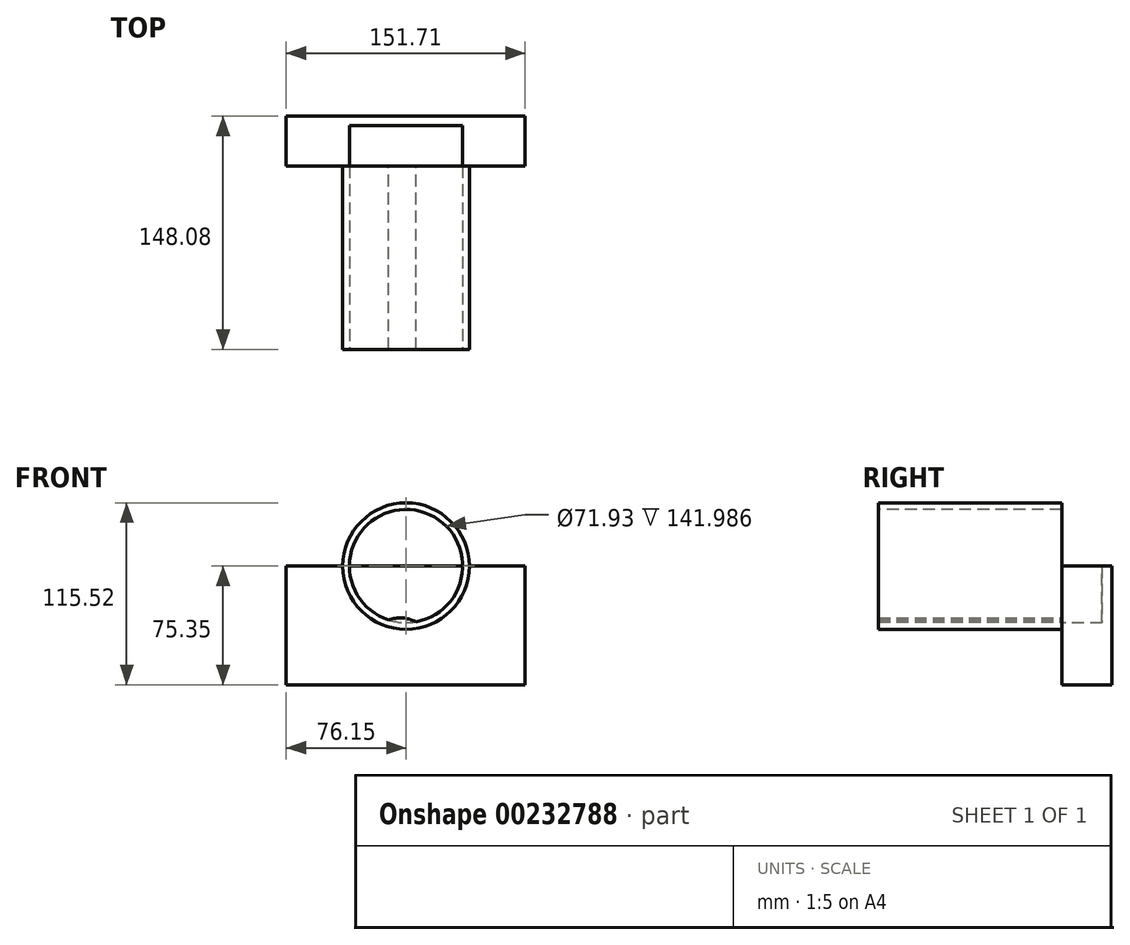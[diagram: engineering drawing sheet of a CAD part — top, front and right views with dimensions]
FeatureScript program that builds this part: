
annotation { "Feature Type Name" : "Feature", "Feature Type Description" : "" }
export const myFeature = defineFeature(function(context is Context, id is Id, definition is map)
    precondition{}
    {
        {
            var Q0;
            Q0=qCreatedBy(makeId("Front.planeOp"),FACE);
            var sketch = newSketch(context, id + "F0", { "sketchPlane" : qUnion([Q0])});
            skCircle(sketch, "E0", {"center": v(0, 0) * mm, "radius": 40.17 * mm});
            skSolve(sketch);
        }
        {
            var Q0;
            Q0=makeQuery(id+"F0.imprint","IMPRINT",FACE,{"disambiguationData":[TD([[makeQuery(id+"F0.imprint","IMPRINT",EDGE,{"derivedFrom":sQuery(id+"F0.wireOp",EDGE,"E0")}),1.0]])]});
            extrude(context, id + "F1", {"entities" : qUnion([Q0]), "depth" : 116.33 * mm});
        }
        {
            var Q0;
            Q0=makeQuery(id+"F1.opExtrude","CAP_FACE",FACE,{"disambiguationData":[OSD([sQuery(id+"F0.wireOp",EDGE,"E0")])],"isStart":false});
            var sketch = newSketch(context, id + "F2", { "sketchPlane" : qUnion([Q0])});
            skCircle(sketch, "E1", {"center": v(0, 0) * mm, "radius": 35.97 * mm});
            skSolve(sketch);
        }
        {
            var Q0;
            Q0=makeQuery(id+"F2.imprint","IMPRINT",FACE,{"disambiguationData":[TD([[makeQuery(id+"F2.imprint","IMPRINT",EDGE,{"derivedFrom":sQuery(id+"F2.wireOp",EDGE,"E1")}),1.0]])]});
            extrude(context, id + "F3", {"entities" : qUnion([Q0]), "operationType" : NewBodyOperationType.REMOVE, "endBound" : BoundingType.THROUGH_ALL, "oppositeDirection" : true, "depth" : 25.4 * mm});
        }
        {
            var Q0;
            Q0=qCreatedBy(makeId("Front.planeOp"),FACE);
            var sketch = newSketch(context, id + "F4", { "sketchPlane" : qUnion([Q0])});
            skLineSegment(sketch, "E2.bottom", {"start": v(0, 0) * mm, "end": v(75.56, 0) * mm});
            skLineSegment(sketch, "E2.top", {"start": v(0, 75.75) * mm, "end": v(75.56, 75.75) * mm});
            skLineSegment(sketch, "E2.left", {"start": v(0, 0) * mm, "end": v(0, 75.75) * mm});
            skLineSegment(sketch, "E2.right", {"start": v(75.56, 0) * mm, "end": v(75.56, 75.75) * mm});
            skLineSegment(sketch, "E3.bottom", {"start": v(75.56, 0) * mm, "end": v(-76.15, 0) * mm});
            skLineSegment(sketch, "E3.top", {"start": v(75.56, -75.35) * mm, "end": v(-76.15, -75.35) * mm});
            skLineSegment(sketch, "E3.left", {"start": v(75.56, 0) * mm, "end": v(75.56, -75.35) * mm});
            skLineSegment(sketch, "E3.right", {"start": v(-76.15, 0) * mm, "end": v(-76.15, -75.35) * mm});
            skLineSegment(sketch, "E4.bottom", {"start": v(0, 0) * mm, "end": v(-75.4, 0) * mm});
            skLineSegment(sketch, "E4.top", {"start": v(0, 75.75) * mm, "end": v(-75.4, 75.75) * mm});
            skLineSegment(sketch, "E4.right", {"start": v(-75.4, 0) * mm, "end": v(-75.4, 75.75) * mm});
            skSolve(sketch);
        }
        {
            var Q0;
            Q0=makeQuery(id+"F4.imprint","IMPRINT",FACE,{"disambiguationData":[TD([[makeQuery(id+"F4.imprint","IMPRINT",EDGE,{"derivedFrom":sQuery(id+"F4.wireOp",EDGE,"E3.top")}),-1.0]])]});
            extrude(context, id + "F5", {"entities" : qUnion([Q0]), "operationType" : NewBodyOperationType.ADD, "oppositeDirection" : true, "depth" : 31.75 * mm});
        }
        {
            var Q0;
            {var subQ0=sQuery(id+"F4.wireOp",EDGE,"E4.bottom");var subQ1=sQuery(id+"F4.wireOp",EDGE,"E3.bottom");Q0=makeQuery(id+"F5.boolean.opBoolean","SPLIT",FACE,{"disambiguationData":[TD([makeQuery(id+"F3.boolean.opBoolean","COPY",FACE,{"derivedFrom":makeQuery(id+"F3.opExtrude","SWEPT_FACE",FACE,{"disambiguationData":[OSD([sQuery(id+"F2.wireOp",EDGE,"E1")])]})})])],"derivedFrom":makeQuery(id+"F5.opExtrude","CAP_FACE",FACE,{"disambiguationData":[OSD([subQ1,sQuery(id+"F4.wireOp",EDGE,"E3.top"),sQuery(id+"F4.wireOp",EDGE,"E3.left"),sQuery(id+"F4.wireOp",EDGE,"E3.right"),subQ0])],"isStart":true})});}
            extrude(context, id + "F6", {"entities" : qUnion([Q0]), "operationType" : NewBodyOperationType.REMOVE, "oppositeDirection" : true, "depth" : 25.65 * mm});
        }
        {
            var Q0;
            {var subQ0=sQuery(id+"F4.wireOp",EDGE,"E3.top");var subQ1=sQuery(id+"F4.wireOp",EDGE,"E4.bottom");var subQ2=sQuery(id+"F4.wireOp",EDGE,"E3.bottom");var subQ3=sQuery(id+"F4.wireOp",EDGE,"E3.right");var subQ4=sQuery(id+"F0.wireOp",EDGE,"E0");var subQ5=sQuery(id+"F4.wireOp",EDGE,"E3.left");Q0=makeQuery(id+"F5.boolean.opBoolean","SPLIT",FACE,{"disambiguationData":[TD([makeQuery(id+"F1.opExtrude","SWEPT_FACE",FACE,{"disambiguationData":[OSD([subQ4])]})])],"derivedFrom":makeQuery(id+"F5.opExtrude","CAP_FACE",FACE,{"disambiguationData":[OSD([subQ2,subQ0,subQ5,subQ3,subQ1])],"isStart":true})});}
            var sketch = newSketch(context, id + "F7", { "sketchPlane" : qUnion([Q0])});
            skCircle(sketch, "E5", {"center": v(-3.75, -54.13) * mm, "radius": 21.22 * mm});
            skSolve(sketch);
        }
        {
            var Q0;
            {var subQ0=sQuery(id+"F7.wireOp",EDGE,"E5");var subQ1=makeQuery(id+"F5.boolean.opBoolean","SPLIT",EDGE,{"disambiguationData":[OD(1.0)],"derivedFrom":makeQuery(id+"F1.opExtrude","CAP_EDGE",EDGE,{"disambiguationData":[OSD([sQuery(id+"F0.wireOp",EDGE,"E0")])],"isStart":true})});var subQ2=makeQuery(id+"F7.imprint","INTERSECT",VERTEX,{"disambiguationData":[OD(0.0)],"derivedFrom":[subQ1,subQ0]});Q0=makeQuery(id+"F7.imprint","IMPRINT",FACE,{"disambiguationData":[TD([[makeQuery(id+"F7.imprint","IMPRINT",EDGE,{"disambiguationData":[TD([[subQ2,-1.0]])],"derivedFrom":subQ0}),1.0]])]});}
            extrude(context, id + "F8", {"entities" : qUnion([Q0]), "operationType" : NewBodyOperationType.ADD, "depth" : 116.33 * mm});
        }
    });
